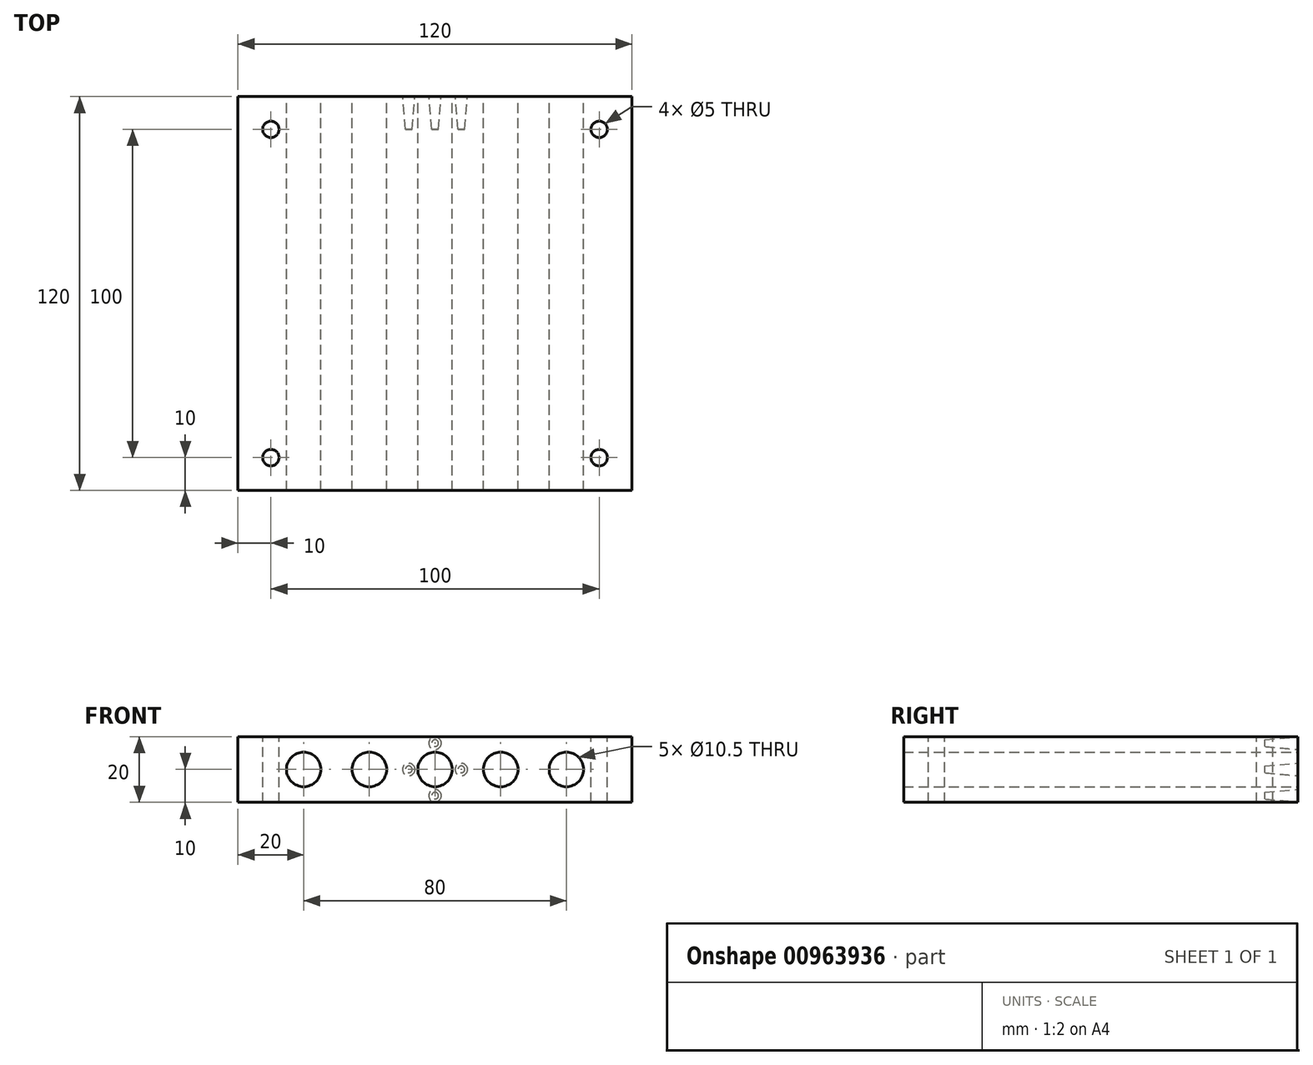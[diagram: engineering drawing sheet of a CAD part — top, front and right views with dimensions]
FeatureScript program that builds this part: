
annotation { "Feature Type Name" : "Feature", "Feature Type Description" : "" }
export const myFeature = defineFeature(function(context is Context, id is Id, definition is map)
    precondition{}
    {
        {
            var Q0;
            Q0=qCreatedBy(makeId("Front.planeOp"),FACE);
            var sketch = newSketch(context, id + "F0", { "sketchPlane" : qUnion([Q0])});
            skCircle(sketch, "E0", {"center": v(0, 10) * mm, "radius": 5.25 * mm});
            skCircle(sketch, "E1", {"center": v(-40, 10) * mm, "radius": 5.25 * mm});
            skLineSegment(sketch, "E2", {"start": v(0, 0) * mm, "end": v(0, 57.15) * mm, "construction": true});
            skCircle(sketch, "E3.MirrorC", {"center": v(40, 10) * mm, "radius": 5.25 * mm});
            skLineSegment(sketch, "E4.bottom", {"start": v(60, 0) * mm, "end": v(-60, 0) * mm});
            skLineSegment(sketch, "E4.top", {"start": v(60, 20) * mm, "end": v(-60, 20) * mm});
            skLineSegment(sketch, "E4.left", {"start": v(60, 0) * mm, "end": v(60, 20) * mm});
            skLineSegment(sketch, "E4.right", {"start": v(-60, 0) * mm, "end": v(-60, 20) * mm});
            skLineSegment(sketch, "E5", {"start": v(60, 10) * mm, "end": v(-60, 10) * mm, "construction": true});
            skCircle(sketch, "E6", {"center": v(0, 10) * mm, "radius": 8 * mm, "construction": true});
            skCircle(sketch, "E7", {"center": v(-8, 10) * mm, "radius": 1.9 * mm});
            skCircle(sketch, "E8.1.0", {"center": v(0, 2) * mm, "radius": 1.9 * mm});
            skCircle(sketch, "E8.2.0", {"center": v(8, 10) * mm, "radius": 1.9 * mm});
            skCircle(sketch, "E8.3.0", {"center": v(0, 18) * mm, "radius": 1.9 * mm});
            skLineSegment(sketch, "E9", {"start": v(-40, 10) * mm, "end": v(0, 10) * mm, "construction": true});
            skCircle(sketch, "E10", {"center": v(-20, 10) * mm, "radius": 5.25 * mm});
            skCircle(sketch, "E11.MirrorC", {"center": v(20, 10) * mm, "radius": 5.25 * mm});
            skSolve(sketch);
        }
        {
            var Q0;
            Q0=makeQuery(id+"F0.imprint","IMPRINT",FACE,{"disambiguationData":[TD([[makeQuery(id+"F0.imprint","IMPRINT",EDGE,{"derivedFrom":sQuery(id+"F0.wireOp",EDGE,"E0")}),-1.0]])]});
            var Q1;
            Q1=makeQuery(id+"F0.imprint","IMPRINT",FACE,{"disambiguationData":[TD([[makeQuery(id+"F0.imprint","IMPRINT",EDGE,{"derivedFrom":sQuery(id+"F0.wireOp",EDGE,"E8.2.0")}),1.0]])]});
            var Q2;
            Q2=makeQuery(id+"F0.imprint","IMPRINT",FACE,{"disambiguationData":[TD([[makeQuery(id+"F0.imprint","IMPRINT",EDGE,{"derivedFrom":sQuery(id+"F0.wireOp",EDGE,"E8.3.0")}),1.0]])]});
            var Q3;
            Q3=makeQuery(id+"F0.imprint","IMPRINT",FACE,{"disambiguationData":[TD([[makeQuery(id+"F0.imprint","IMPRINT",EDGE,{"derivedFrom":sQuery(id+"F0.wireOp",EDGE,"E7")}),1.0]])]});
            var Q4;
            Q4=makeQuery(id+"F0.imprint","IMPRINT",FACE,{"disambiguationData":[TD([[makeQuery(id+"F0.imprint","IMPRINT",EDGE,{"derivedFrom":sQuery(id+"F0.wireOp",EDGE,"E8.1.0")}),1.0]])]});
            extrude(context, id + "F1", {"entities" : qUnion([Q0, Q1, Q2, Q3, Q4]), "depth" : 120 * mm, "offsetDistance" : 25 * mm});
        }
        {
            var Q0;
            Q0=makeQuery(id+"F1.opExtrude","SWEPT_FACE",FACE,{"disambiguationData":[OSD([sQuery(id+"F0.wireOp",EDGE,"E4.top")])]});
            var sketch = newSketch(context, id + "F2", { "sketchPlane" : qUnion([Q0])});
            skLineSegment(sketch, "E12.bottom", {"start": v(50, -10) * mm, "end": v(-50, -10) * mm, "construction": true});
            skLineSegment(sketch, "E12.top", {"start": v(50, -110) * mm, "end": v(-50, -110) * mm, "construction": true});
            skLineSegment(sketch, "E12.left", {"start": v(50, -10) * mm, "end": v(50, -110) * mm, "construction": true});
            skLineSegment(sketch, "E12.right", {"start": v(-50, -10) * mm, "end": v(-50, -110) * mm, "construction": true});
            skPoint(sketch, "E12.middle", {"position": v(0, -60) * mm});
            skPoint(sketch, "E12.middle.positionSnap0", {"position": v(0, -120) * mm});
            skPoint(sketch, "E12.middle.positionSnap1", {"position": v(-60, -60) * mm});
            skPoint(sketch, "E12.centerSnap0", {"position": v(0, -120) * mm});
            skPoint(sketch, "E12.centerSnap1", {"position": v(-60, -60) * mm});
            skSolve(sketch);
        }
        {
            var Q0;
            Q0=sQuery(id+"F2.wireOp",VERTEX,"E12.right.start");
            var Q1;
            Q1=sQuery(id+"F2.wireOp",VERTEX,"E12.bottom.start");
            var Q2;
            Q2=sQuery(id+"F2.wireOp",VERTEX,"E12.right.end");
            var Q3;
            Q3=sQuery(id+"F2.wireOp",VERTEX,"E12.left.end");
            var Q4;
            Q4=makeQuery(id+"F1.opExtrude","SWEPT_BODY",BODY,{"disambiguationData":[OSD([sQuery(id+"F0.wireOp",EDGE,"E0"),sQuery(id+"F0.wireOp",EDGE,"E1"),sQuery(id+"F0.wireOp",EDGE,"E3.MirrorC"),sQuery(id+"F0.wireOp",EDGE,"E4.bottom"),sQuery(id+"F0.wireOp",EDGE,"E4.top"),sQuery(id+"F0.wireOp",EDGE,"E4.left"),sQuery(id+"F0.wireOp",EDGE,"E4.right")])]});
            hole(context, id + "F3", {"style" : HoleStyle.SIMPLE, "endStyle" : HoleEndStyle.THROUGH, "holeDiameter" : 5 * mm, "majorDiameter" : 5 * mm, "isTappedThrough" : true, "tappedDepth" : 12 * mm, "tapClearance" : 3, "locations" : qUnion([Q0, Q1, Q2, Q3]), "scope" : qUnion([Q4])});
        }
        {
            var Q0;
            Q0=makeQuery(id+"F0.imprint","IMPRINT",FACE,{"disambiguationData":[TD([[makeQuery(id+"F0.imprint","IMPRINT",EDGE,{"derivedFrom":sQuery(id+"F0.wireOp",EDGE,"E8.2.0")}),1.0]])]});
            var Q1;
            Q1=makeQuery(id+"F0.imprint","IMPRINT",FACE,{"disambiguationData":[TD([[makeQuery(id+"F0.imprint","IMPRINT",EDGE,{"derivedFrom":sQuery(id+"F0.wireOp",EDGE,"E8.3.0")}),1.0]])]});
            var Q2;
            Q2=makeQuery(id+"F0.imprint","IMPRINT",FACE,{"disambiguationData":[TD([[makeQuery(id+"F0.imprint","IMPRINT",EDGE,{"derivedFrom":sQuery(id+"F0.wireOp",EDGE,"E7")}),1.0]])]});
            var Q3;
            Q3=makeQuery(id+"F0.imprint","IMPRINT",FACE,{"disambiguationData":[TD([[makeQuery(id+"F0.imprint","IMPRINT",EDGE,{"derivedFrom":sQuery(id+"F0.wireOp",EDGE,"E8.1.0")}),1.0]])]});
            extrude(context, id + "F4", {"entities" : qUnion([Q0, Q1, Q2, Q3]), "operationType" : NewBodyOperationType.REMOVE, "depth" : 10 * mm, "offsetDistance" : 25 * mm, "hasDraft" : true, "draftAngle" : 5 * degree, "draftPullDirection" : true});
        }
    });
